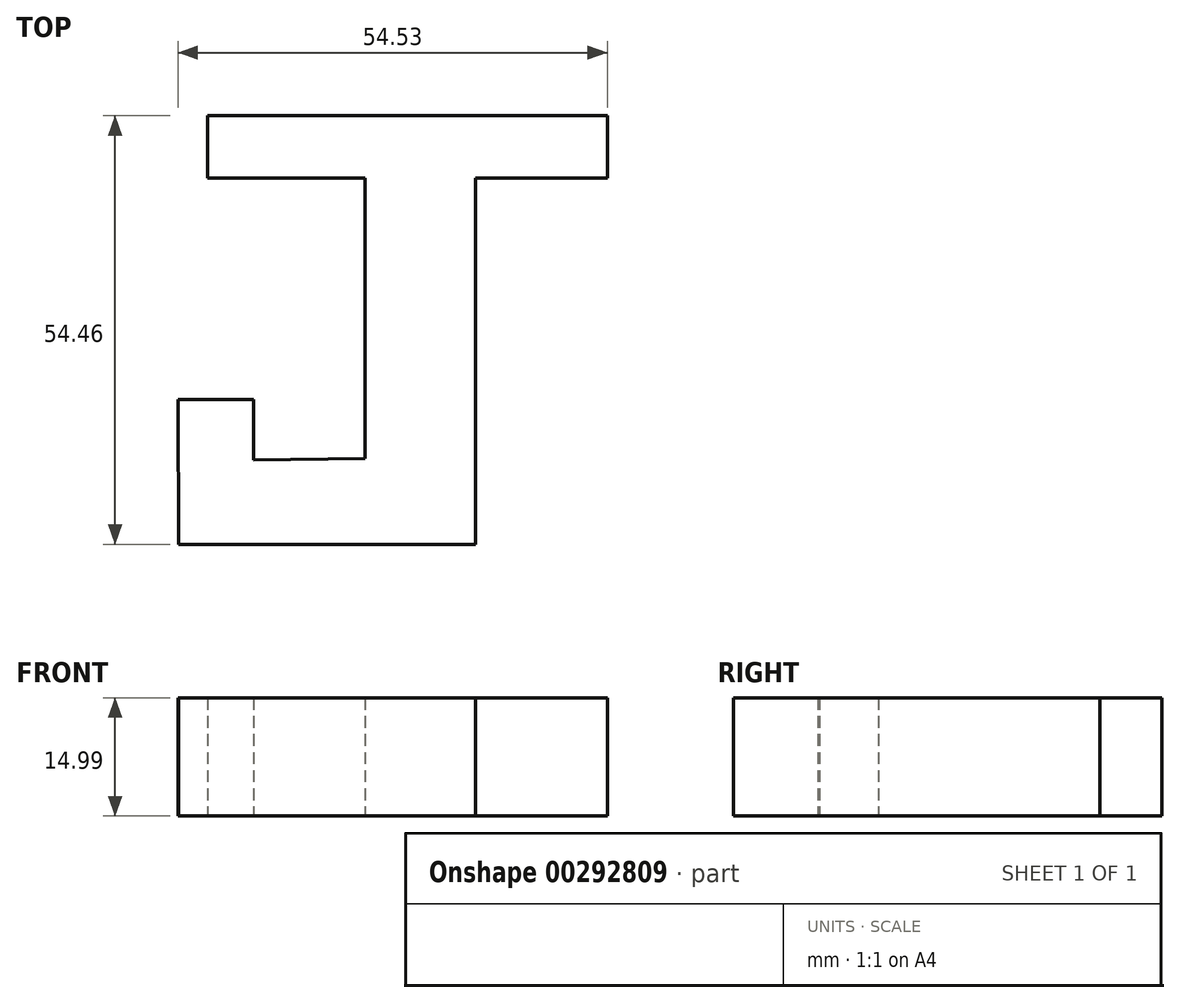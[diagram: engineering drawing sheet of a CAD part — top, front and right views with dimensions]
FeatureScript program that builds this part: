
annotation { "Feature Type Name" : "Feature", "Feature Type Description" : "" }
export const myFeature = defineFeature(function(context is Context, id is Id, definition is map)
    precondition{}
    {
        {
            var Q0;
            Q0=qCreatedBy(makeId("Top.planeOp"),FACE);
            var sketch = newSketch(context, id + "F0", { "sketchPlane" : qUnion([Q0])});
            skLineSegment(sketch, "E0", {"start": v(-65.66, 65.06) * mm, "end": v(-14.86, 65.06) * mm});
            skLineSegment(sketch, "E1", {"start": v(-65.66, 65.06) * mm, "end": v(-65.66, 57.16) * mm});
            skLineSegment(sketch, "E2", {"start": v(-14.86, 65.06) * mm, "end": v(-14.86, 57.16) * mm});
            skLineSegment(sketch, "E3", {"start": v(-31.62, 57.16) * mm, "end": v(-31.62, 10.6) * mm});
            skLineSegment(sketch, "E4", {"start": v(-31.62, 10.6) * mm, "end": v(-69.35, 10.6) * mm});
            skLineSegment(sketch, "E5", {"start": v(-45.67, 57.16) * mm, "end": v(-45.67, 21.53) * mm});
            skLineSegment(sketch, "E6", {"start": v(-69.35, 10.6) * mm, "end": v(-69.4, 29.02) * mm});
            skLineSegment(sketch, "E7", {"start": v(-69.4, 29.02) * mm, "end": v(-59.83, 29.02) * mm});
            skLineSegment(sketch, "E8", {"start": v(-59.83, 29.02) * mm, "end": v(-59.83, 21.32) * mm});
            skLineSegment(sketch, "E9", {"start": v(-59.83, 21.32) * mm, "end": v(-45.67, 21.53) * mm});
            skLineSegment(sketch, "E10", {"start": v(-65.66, 57.16) * mm, "end": v(-45.67, 57.16) * mm});
            skLineSegment(sketch, "E11", {"start": v(-31.62, 57.16) * mm, "end": v(-14.86, 57.16) * mm});
            skSolve(sketch);
        }
        {
            var Q0;
            Q0=makeQuery(id+"F0.imprint","IMPRINT",FACE,{"disambiguationData":[TD([[makeQuery(id+"F0.imprint","IMPRINT",EDGE,{"derivedFrom":sQuery(id+"F0.wireOp",EDGE,"E0")}),-1.0]])]});
            extrude(context, id + "F1", {"entities" : qUnion([Q0]), "depth" : 15 * mm});
        }
    });
